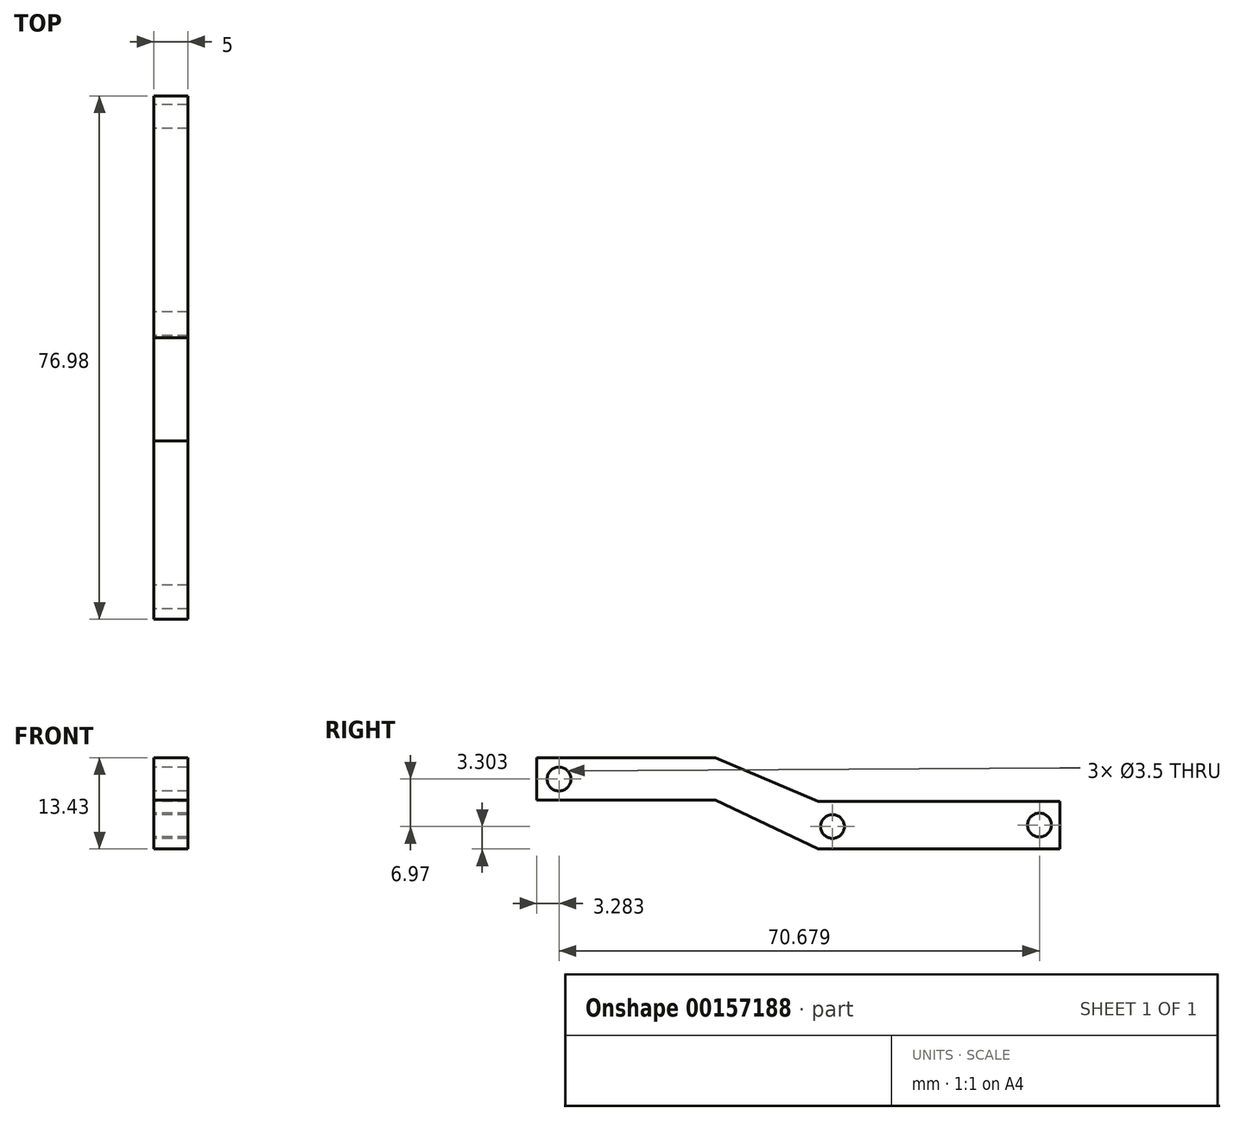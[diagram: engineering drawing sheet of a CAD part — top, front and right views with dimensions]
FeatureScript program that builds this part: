
annotation { "Feature Type Name" : "Feature", "Feature Type Description" : "" }
export const myFeature = defineFeature(function(context is Context, id is Id, definition is map)
    precondition{}
    {
        {
            var Q0;
            Q0=qCreatedBy(makeId("Right.planeOp"),FACE);
            var sketch = newSketch(context, id + "F0", { "sketchPlane" : qUnion([Q0])});
            skLineSegment(sketch, "E0.bottom", {"start": v(30.61, 0) * mm, "end": v(-4.95, 0) * mm});
            skLineSegment(sketch, "E0.top", {"start": v(30.61, 6.98) * mm, "end": v(-4.95, 6.98) * mm});
            skLineSegment(sketch, "E0.left", {"start": v(30.61, 0) * mm, "end": v(30.61, 6.98) * mm});
            skLineSegment(sketch, "E1", {"start": v(-4.95, 0) * mm, "end": v(-20.08, 7.2) * mm});
            skLineSegment(sketch, "E2", {"start": v(-4.95, 6.98) * mm, "end": v(-20.1, 13.43) * mm});
            skLineSegment(sketch, "E3.bottom", {"start": v(-20.1, 13.43) * mm, "end": v(-46.37, 13.43) * mm});
            skLineSegment(sketch, "E3.top", {"start": v(-20.08, 7.2) * mm, "end": v(-46.37, 7.2) * mm});
            skLineSegment(sketch, "E3.right", {"start": v(-46.37, 13.43) * mm, "end": v(-46.37, 7.2) * mm});
            skLineSegment(sketch, "E4", {"start": v(-20.08, 7.2) * mm, "end": v(-20.08, 7.2) * mm});
            skCircle(sketch, "E5", {"center": v(27.6, 3.51) * mm, "radius": 1.75 * mm});
            skCircle(sketch, "E6", {"center": v(-2.86, 3.3) * mm, "radius": 1.75 * mm});
            skCircle(sketch, "E7", {"center": v(-43.09, 10.27) * mm, "radius": 1.75 * mm});
            skSolve(sketch);
        }
        {
            var Q0;
            Q0 = qSketchRegion(id + "F0", true);
            extrude(context, id + "F1", {"entities" : qUnion([Q0]), "depth" : 5 * mm});
        }
    });
